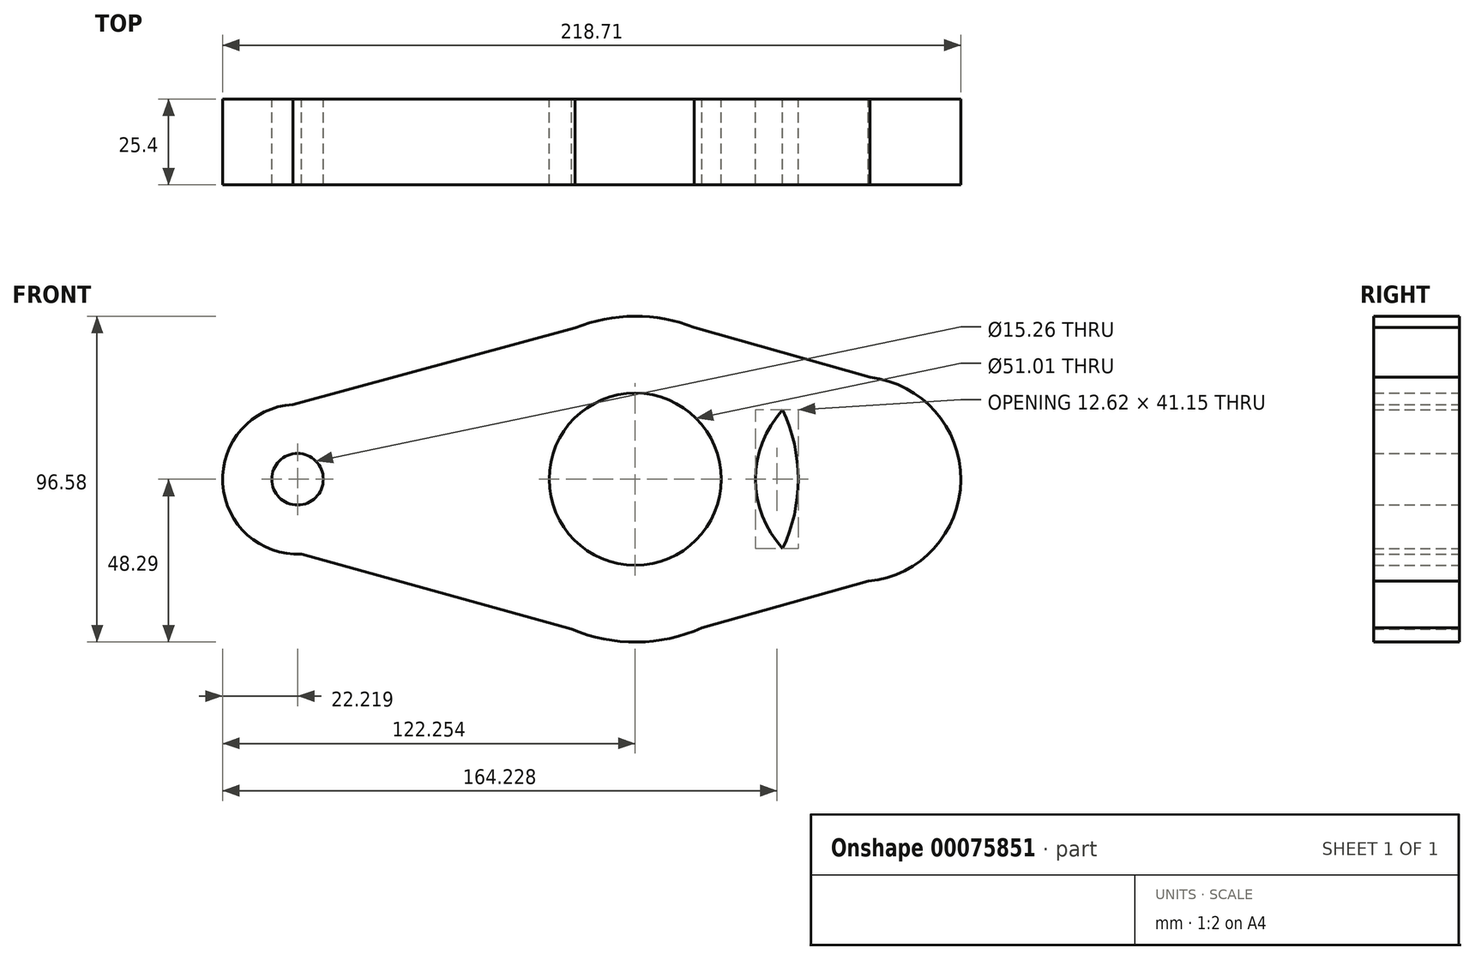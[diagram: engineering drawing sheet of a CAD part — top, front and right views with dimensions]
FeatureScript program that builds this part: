
annotation { "Feature Type Name" : "Feature", "Feature Type Description" : "" }
export const myFeature = defineFeature(function(context is Context, id is Id, definition is map)
    precondition{}
    {
        {
            var Q0;
            Q0=qCreatedBy(makeId("Front.planeOp"),FACE);
            var sketch = newSketch(context, id + "F0", { "sketchPlane" : qUnion([Q0])});
            skCircle(sketch, "E0", {"center": v(-78.64, 0) * mm, "radius": 22.22 * mm});
            skCircle(sketch, "E1", {"center": v(21.4, 0) * mm, "radius": 48.29 * mm});
            skCircle(sketch, "E2", {"center": v(87.46, 0) * mm, "radius": 30.4 * mm});
            skLineSegment(sketch, "E3", {"start": v(30.22, 47.47) * mm, "end": v(90.95, 30.2) * mm});
            skLineSegment(sketch, "E4", {"start": v(41.15, -44.06) * mm, "end": v(90.48, -30.25) * mm});
            skCircle(sketch, "E5", {"center": v(21.4, 0) * mm, "radius": 25.5 * mm});
            skLineSegment(sketch, "E6", {"start": v(-77.45, -22.19) * mm, "end": v(2.53, -44.45) * mm});
            skLineSegment(sketch, "E7", {"start": v(-80.02, 22.18) * mm, "end": v(3.55, 44.87) * mm});
            skCircle(sketch, "E8", {"center": v(-78.64, 0) * mm, "radius": 7.63 * mm});
            skSolve(sketch);
        }
        {
            var Q0;
            Q0 = qSketchRegion(id + "F0", true);
            extrude(context, id + "F1", {"entities" : qUnion([Q0]), "depth" : 25.4 * mm});
        }
    });
